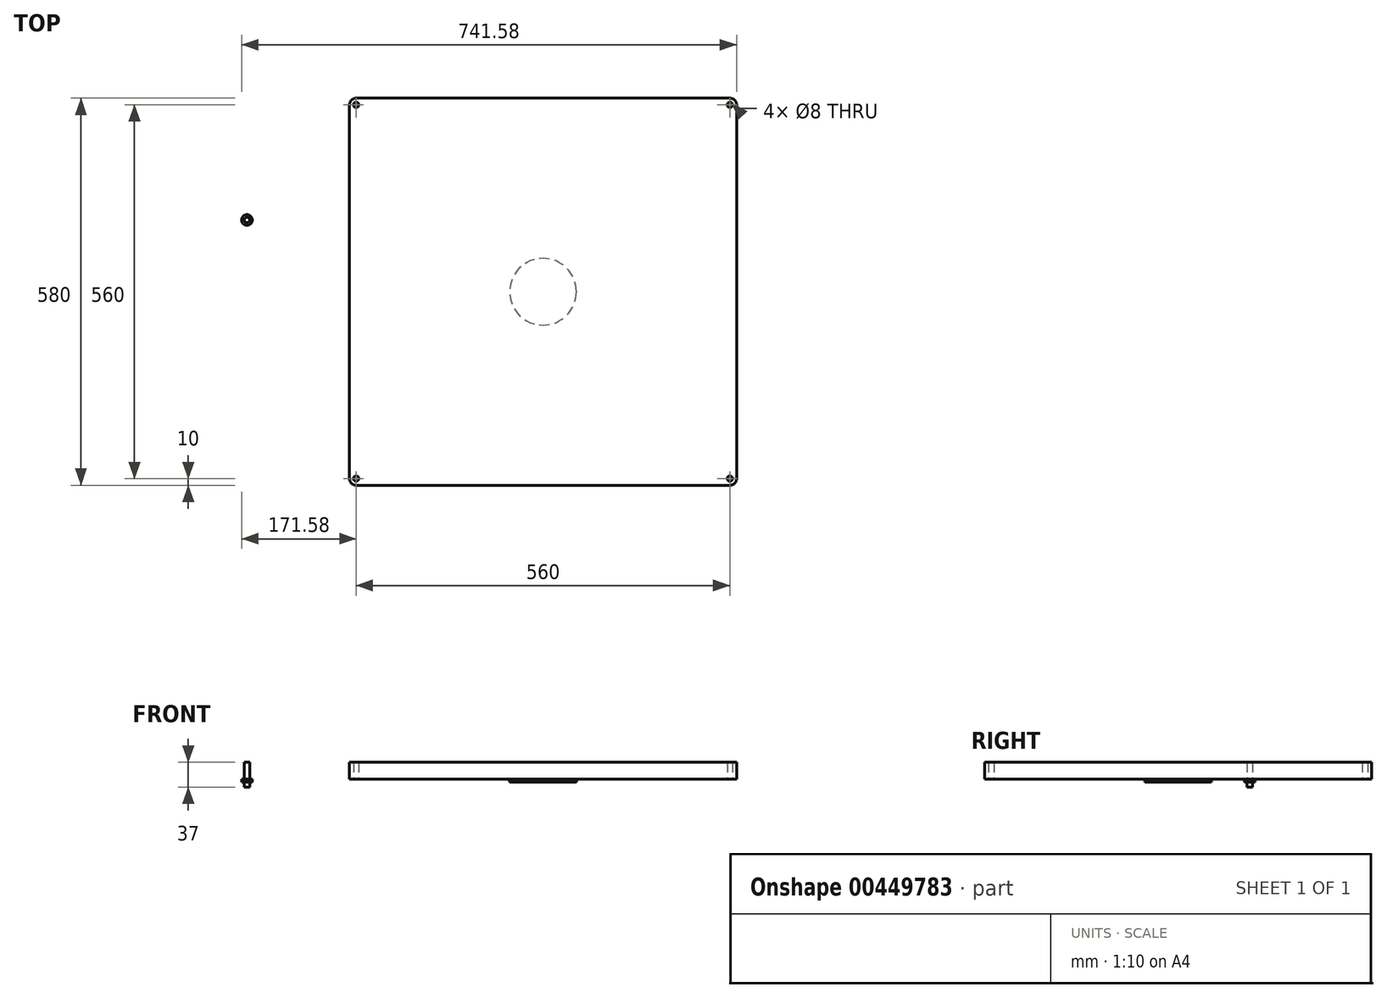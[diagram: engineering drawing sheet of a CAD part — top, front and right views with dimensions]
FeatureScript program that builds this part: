
annotation { "Feature Type Name" : "Feature", "Feature Type Description" : "" }
export const myFeature = defineFeature(function(context is Context, id is Id, definition is map)
    precondition{}
    {
        {
            var Q0;
            Q0=qCreatedBy(makeId("Top.planeOp"),FACE);
            var sketch = newSketch(context, id + "F0", { "sketchPlane" : qUnion([Q0])});
            skLineSegment(sketch, "E0", {"start": v(0, 0) * mm, "end": v(0, 289.69) * mm, "construction": true});
            skLineSegment(sketch, "E1", {"start": v(0, 0) * mm, "end": v(273.74, 0) * mm, "construction": true});
            skLineSegment(sketch, "E2.bottom", {"start": v(280, 290) * mm, "end": v(-280, 290) * mm});
            skLineSegment(sketch, "E2.top", {"start": v(280, -290) * mm, "end": v(-280, -290) * mm});
            skLineSegment(sketch, "E2.left", {"start": v(290, 280) * mm, "end": v(290, -280) * mm});
            skLineSegment(sketch, "E2.right", {"start": v(-290, 280) * mm, "end": v(-290, -280) * mm});
            skPoint(sketch, "E2.middle", {"position": v(0, 0) * mm});
            skCircle(sketch, "E3", {"center": v(-280, 280) * mm, "radius": 4 * mm});
            skCircle(sketch, "E4", {"center": v(280, 280) * mm, "radius": 4 * mm});
            skCircle(sketch, "E5", {"center": v(280, -280) * mm, "radius": 4 * mm});
            skCircle(sketch, "E6", {"center": v(-280, -280) * mm, "radius": 4 * mm});
            skPoint(sketch, "E7.visualSharp", {"position": v(-290, 290) * mm});
            skArc(sketch, "E7.filletArc", {"start": v(-280, 290) * mm, "mid": v(-287.07, 287.07) * mm, "end": v(-290, 280) * mm});
            skPoint(sketch, "E8.visualSharp", {"position": v(290, 290) * mm});
            skArc(sketch, "E8.filletArc", {"start": v(290, 280) * mm, "mid": v(287.07, 287.07) * mm, "end": v(280, 290) * mm});
            skPoint(sketch, "E9.visualSharp", {"position": v(290, -290) * mm});
            skArc(sketch, "E9.filletArc", {"start": v(280, -290) * mm, "mid": v(287.07, -287.07) * mm, "end": v(290, -280) * mm});
            skPoint(sketch, "E10.visualSharp", {"position": v(-290, -290) * mm});
            skArc(sketch, "E10.filletArc", {"start": v(-290, -280) * mm, "mid": v(-287.07, -287.07) * mm, "end": v(-280, -290) * mm});
            skCircle(sketch, "E11", {"center": v(0, 0) * mm, "radius": 50 * mm});
            skSolve(sketch);
        }
        {
            var Q0;
            Q0=makeQuery(id+"F0.imprint","IMPRINT",FACE,{"disambiguationData":[TD([[makeQuery(id+"F0.imprint","IMPRINT",EDGE,{"derivedFrom":sQuery(id+"F0.wireOp",EDGE,"E2.bottom")}),1.0]])]});
            var Q1;
            Q1=makeQuery(id+"F0.imprint","IMPRINT",FACE,{"disambiguationData":[TD([[makeQuery(id+"F0.imprint","IMPRINT",EDGE,{"derivedFrom":sQuery(id+"F0.wireOp",EDGE,"E11")}),1.0]])]});
            extrude(context, id + "F1", {"entities" : qUnion([Q0, Q1]), "depth" : 25 * mm});
        }
        {
            var Q0;
            Q0=qCreatedBy(makeId("Top.planeOp"),FACE);
            var sketch = newSketch(context, id + "F2", { "sketchPlane" : qUnion([Q0])});
            skCircle(sketch, "E12", {"center": v(-443.58, 107.45) * mm, "radius": 4 * mm});
            skCircle(sketch, "E13", {"center": v(-443.58, 107.45) * mm, "radius": 8 * mm});
            skSolve(sketch);
        }
        {
            var Q0;
            Q0=makeQuery(id+"F2.imprint","IMPRINT",FACE,{"disambiguationData":[TD([[makeQuery(id+"F2.imprint","IMPRINT",EDGE,{"derivedFrom":sQuery(id+"F2.wireOp",EDGE,"E12")}),1.0]])]});
            extrude(context, id + "F3", {"entities" : qUnion([Q0]), "depth" : 25 * mm, "hasSecondDirection" : true, "secondDirectionOppositeDirection" : true, "secondDirectionDepth" : 12 * mm});
        }
        {
            var Q0;
            Q0=makeQuery(id+"F2.imprint","IMPRINT",FACE,{"disambiguationData":[TD([[makeQuery(id+"F2.imprint","IMPRINT",EDGE,{"derivedFrom":sQuery(id+"F2.wireOp",EDGE,"E12")}),-1.0]])]});
            extrude(context, id + "F4", {"entities" : qUnion([Q0]), "operationType" : NewBodyOperationType.ADD, "oppositeDirection" : true, "depth" : 5 * mm});
        }
        {
            var Q0;
            Q0=makeQuery(id+"F0.imprint","IMPRINT",FACE,{"disambiguationData":[TD([[makeQuery(id+"F0.imprint","IMPRINT",EDGE,{"derivedFrom":sQuery(id+"F0.wireOp",EDGE,"E11")}),1.0]])]});
            extrude(context, id + "F5", {"entities" : qUnion([Q0]), "operationType" : NewBodyOperationType.ADD, "oppositeDirection" : true, "depth" : 5 * mm});
        }
    });
